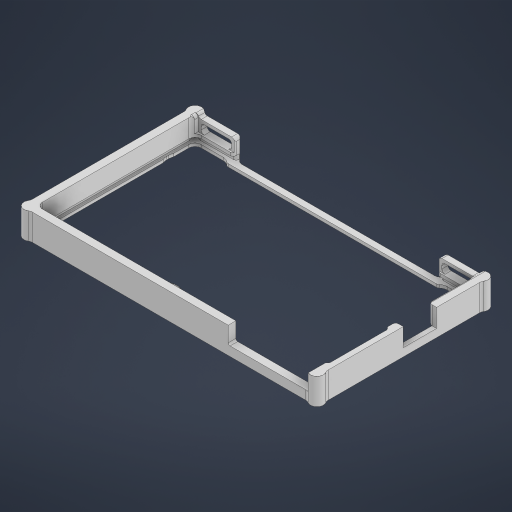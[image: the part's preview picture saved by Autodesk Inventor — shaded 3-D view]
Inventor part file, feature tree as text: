
AUTODESK INVENTOR PART (.ipt)
format: ipt  version: 2024 (Build 280153000, 153)  size: 726,016 bytes
history: native  units: mm
features: projected_geometry x12, extrude x11, sketch x10, fillet x5, other x1, mirror x1
ambient origin geometry x8: Origin, YZ Plane, XZ Plane, XY Plane, X Axis, Y Axis, Z Axis, Center Point
bodies: Body1 (feature_tree)
feature tree (40):
  other  "Těleso1"
  sketch  "Náčrt1"
  extrude  "Vysunutí1"  Depth=95.0mm
  extrude  "Vysunutí2"  Depth=55.0mm
  extrude  "Vysunutí3"  Depth=0.5mm
  extrude  "Vysunutí8"  Depth=10.0mm
  extrude  "Vysunutí4"  Depth=17.5mm
  extrude  "Vysunutí5"  Depth=8.5mm
  extrude  "Vysunutí7"  Depth=5.0mm
  extrude  "Vysunutí9"  Depth=1.0mm
  extrude  "Vysunutí11"  Depth=1.5mm
  fillet  "Zaoblení4"  Radius=1.0mm
  mirror  "Zrcadlit1"
  fillet  "Zaoblení1"  Radius=2.6mm
  fillet  "Zaoblení2"  Radius=15.0mm
  extrude  "Vysunutí10"  Depth=15.0mm
  fillet  "Zaoblení3"  Radius=25.5mm
  extrude  "Vysunutí12"  Depth=3.9mm
  fillet  "Zaoblení5"  Radius=30.1mm
  sketch  "Náčrt2"
  projected_geometry  "Promítnutá smyčka1"
  projected_geometry  "Promítnutá smyčka2"
  sketch  "Náčrt3"
  sketch  "Náčrt4"
  projected_geometry  "Promítnutá smyčka3"
  sketch  "Náčrt6"
  projected_geometry  "Promítnutá smyčka5"
  sketch  "Náčrt7"
  projected_geometry  "Promítnutá smyčka6"
  projected_geometry  "Promítnutá smyčka7"
  sketch  "Náčrt8"
  projected_geometry  "Promítnutá smyčka8"
  sketch  "Náčrt10"
  projected_geometry  "Promítnutá smyčka9"
  sketch  "Náčrt12"
  projected_geometry  "Promítnutá smyčka11"
  sketch  "Náčrt13"
  projected_geometry  "Promítnutá smyčka12"
  projected_geometry  "Promítnutá smyčka13"
  projected_geometry  "Promítnutá smyčka14"
